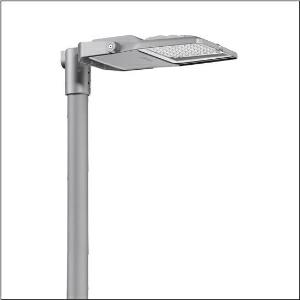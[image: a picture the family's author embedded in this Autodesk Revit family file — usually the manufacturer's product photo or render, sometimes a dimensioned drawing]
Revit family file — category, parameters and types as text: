
# Revit family: floodlight_fl_21_iq_mini___pl33t_5xa7772c4f3a_1e48
name_source: partatom
category: Lighting Fixtures
units: mm (PartAtom-declared; Revit-internal decimal feet)

## family parameters
Cut with Voids When Loaded = No
Host = Face
Light Source = No
Part Type = Normal
Room Calculation Point = No
Round Connector Dimension = Use Diameter
Shared = No

## types (1)
- --- (1 x LED, 12570 lm, 87.2 W, 4000K)
    Apparent Load = 87 VA
    CIE Flux Codes = 26 75 99 100 100
    Color Rendering = 70
    Color Temperature = 4000K
    Default Elevation = 1800 mm
    Description = Floodlight FL 21 iQ mini, floodlight, primary light control with lens, of PMMA, primary optical cover: protective disc, of toughened safety glass, transparent, light distribution: PL33T, light emission: direct distribution, installation type: surface-mounted, LED, High Power LED, rated luminous flux: 12.570lm, luminous efficacy: 144lm/W, light colour: 740, colour temperature: 4000K, control: Auto-Match, Temp-Guard, Night-Set, Smart-Wire, Desk-Remote (wireless, voltage-free reading and setting of iQ features in the workshop via application-optimized NFC function/RFID function), optimised constant luminous flux control (CLO 2.0), Light-Fading, Lumen-Switch, with terminal, 6-pole, mains connection: 220..240V, AC, 50/60Hz, start of lifetime: 87W, end of service life: 92W, reduction: 40W, luminaire housing, of diecast aluminium, powder-coated, Siteco® metallic grey (DB 702S), corrosivity category C5 mid according to DIN EN ISO 12944, sealing non-destructively replaceable, please order mast flange separately, mast bracket, of steel, galvanised, powder-coated, protection rating (complete): IP66, insulation class (complete): insulation class II (safety insulation), certification: CE, ENEC, VDE, protection symbol: D, impact resistance: IK08, permissible operating ambient temperature: -40..+40°C, permissible operating ambient temperature for outdoor applications: -40..+50°C, standard: DIN EN 12944, LABS conformity tested according to VDMA 24364:2018-05, packaging unit: 1 piece

Light Distribution: PL33T
    Height = 70 mm
    Lamp = 1 x LED
    Lamp Light Flux = 12570 lm
    Lamp Power = 87.2 W
    Lamp count = 1
    Length = 485 mm
    Luminous efficacy = 144 lm/W
    Manufacturer = Siteco
    ModVariant = No
    Model = 5XA7772C4F3A
    Number of Poles = 1
    OnlyDefault = Yes
    Power Factor = 1
    Product Name = Floodlight FL 21 iQ mini | PL33T
    Product group = floodlight | pylon annexe
    ProductGroupID = 6200
    Protection Class = Protection class II
    Protection Degree = IP 66
    RLX_Detail_Level = 1
    RLX_Emergency_Light_Flux = 0 lm
    RLX_Emergency_Type = 0
    RLX_Emergency_Type_DB = No
    RlxData = <blob elided: 101241 chars, md5=c8a396f3>
    Socket = socket
    Standby Power = 0 W
    System Light Flux = 12570 lm
    System Power = 87 W
    Type Comments = factory setting: luminous flux: 100 % | dim-lin: 254 | 456 mA
    Type Image = l_1007125.jpg
    URL = http://relux.com
    VarID = @adj_119681
    Voltage = 0 V
    Weight = 0.00 kg
    Width = 337 mm

## geometry (parser evidence)
native form markers: Blend x4, Sweep x12
no freeform markers — native parametric forms only
